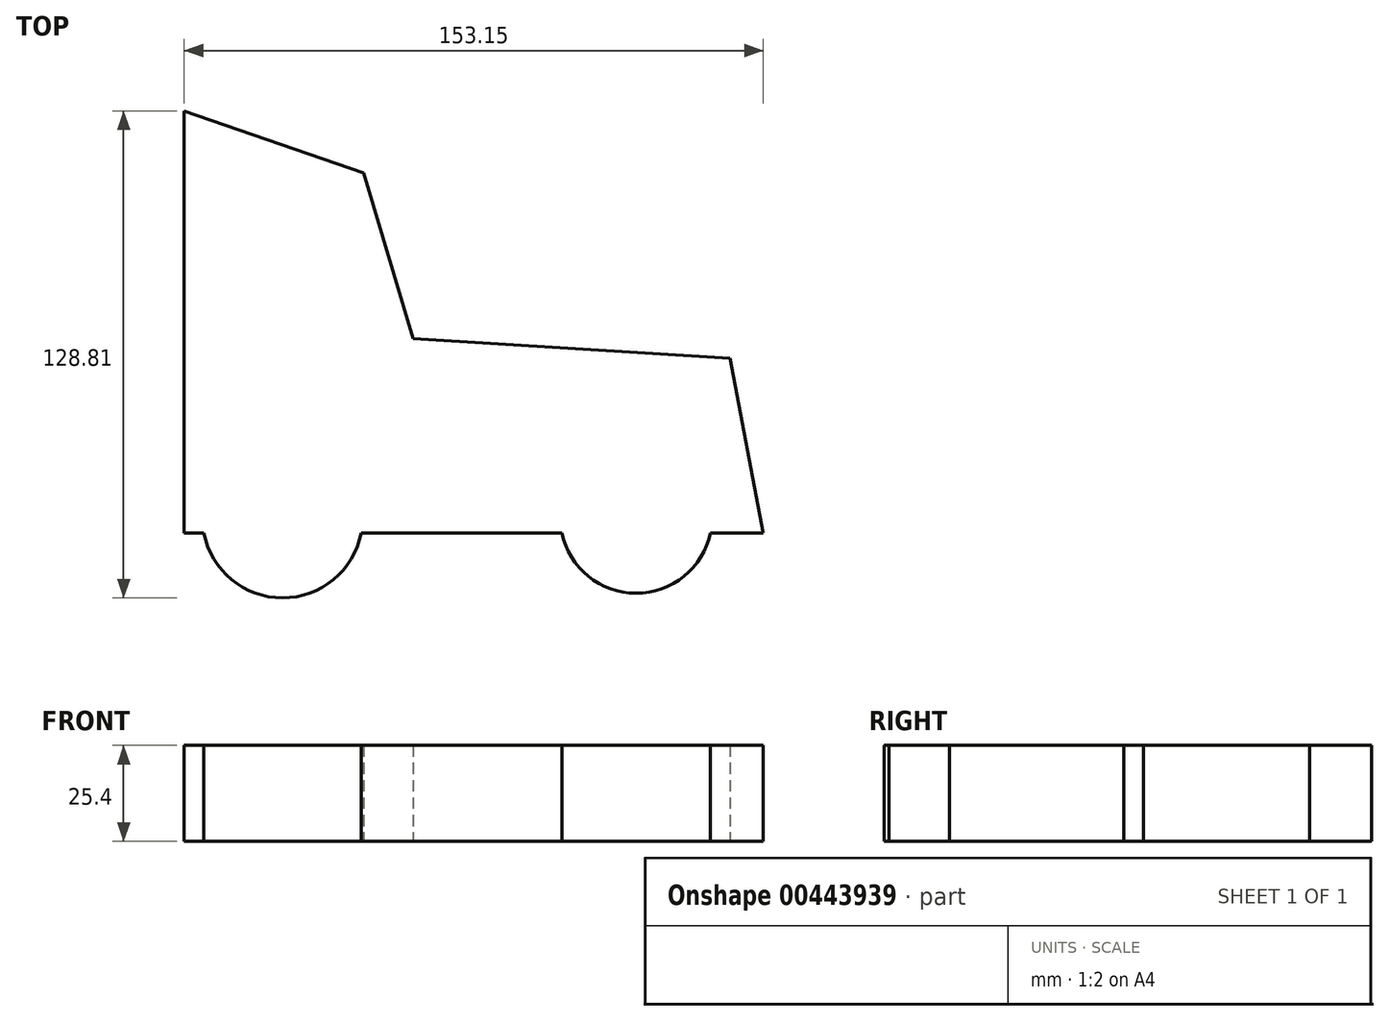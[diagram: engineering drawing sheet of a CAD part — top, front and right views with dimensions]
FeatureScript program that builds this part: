
annotation { "Feature Type Name" : "Feature", "Feature Type Description" : "" }
export const myFeature = defineFeature(function(context is Context, id is Id, definition is map)
    precondition{}
    {
        {
            var Q0;
            Q0=qCreatedBy(makeId("Top.planeOp"),FACE);
            var sketch = newSketch(context, id + "F0", { "sketchPlane" : qUnion([Q0])});
            skLineSegment(sketch, "E0", {"start": v(-75.76, -75.43) * mm, "end": v(77.4, -75.43) * mm});
            skLineSegment(sketch, "E1", {"start": v(77.4, -75.43) * mm, "end": v(68.56, -29.29) * mm});
            skLineSegment(sketch, "E2", {"start": v(68.56, -29.29) * mm, "end": v(-15.22, -24.05) * mm});
            skLineSegment(sketch, "E3", {"start": v(-15.22, -24.05) * mm, "end": v(-28.3, 19.8) * mm});
            skLineSegment(sketch, "E4", {"start": v(-75.76, -75.43) * mm, "end": v(-75.76, 36.16) * mm});
            skLineSegment(sketch, "E5", {"start": v(-75.76, 36.16) * mm, "end": v(-28.3, 19.8) * mm});
            skSolve(sketch);
        }
        {
            var Q0;
            Q0=qSketchRegion(id+"F0",true);
            extrude(context, id + "F1", {"entities" : qUnion([Q0]), "depth" : 25.4 * mm});
        }
        {
            var Q0;
            Q0=qCreatedBy(makeId("Top.planeOp"),FACE);
            var sketch = newSketch(context, id + "F2", { "sketchPlane" : qUnion([Q0])});
            skCircle(sketch, "E6", {"center": v(-49.77, -71.5) * mm, "radius": 21.15 * mm});
            skCircle(sketch, "E7", {"center": v(43.75, -71.33) * mm, "radius": 20.08 * mm});
            skSolve(sketch);
        }
        {
            var Q0;
            Q0=qSketchRegion(id+"F2",true);
            extrude(context, id + "F3", {"entities" : qUnion([Q0]), "operationType" : NewBodyOperationType.ADD, "depth" : 25.4 * mm});
        }
    });
